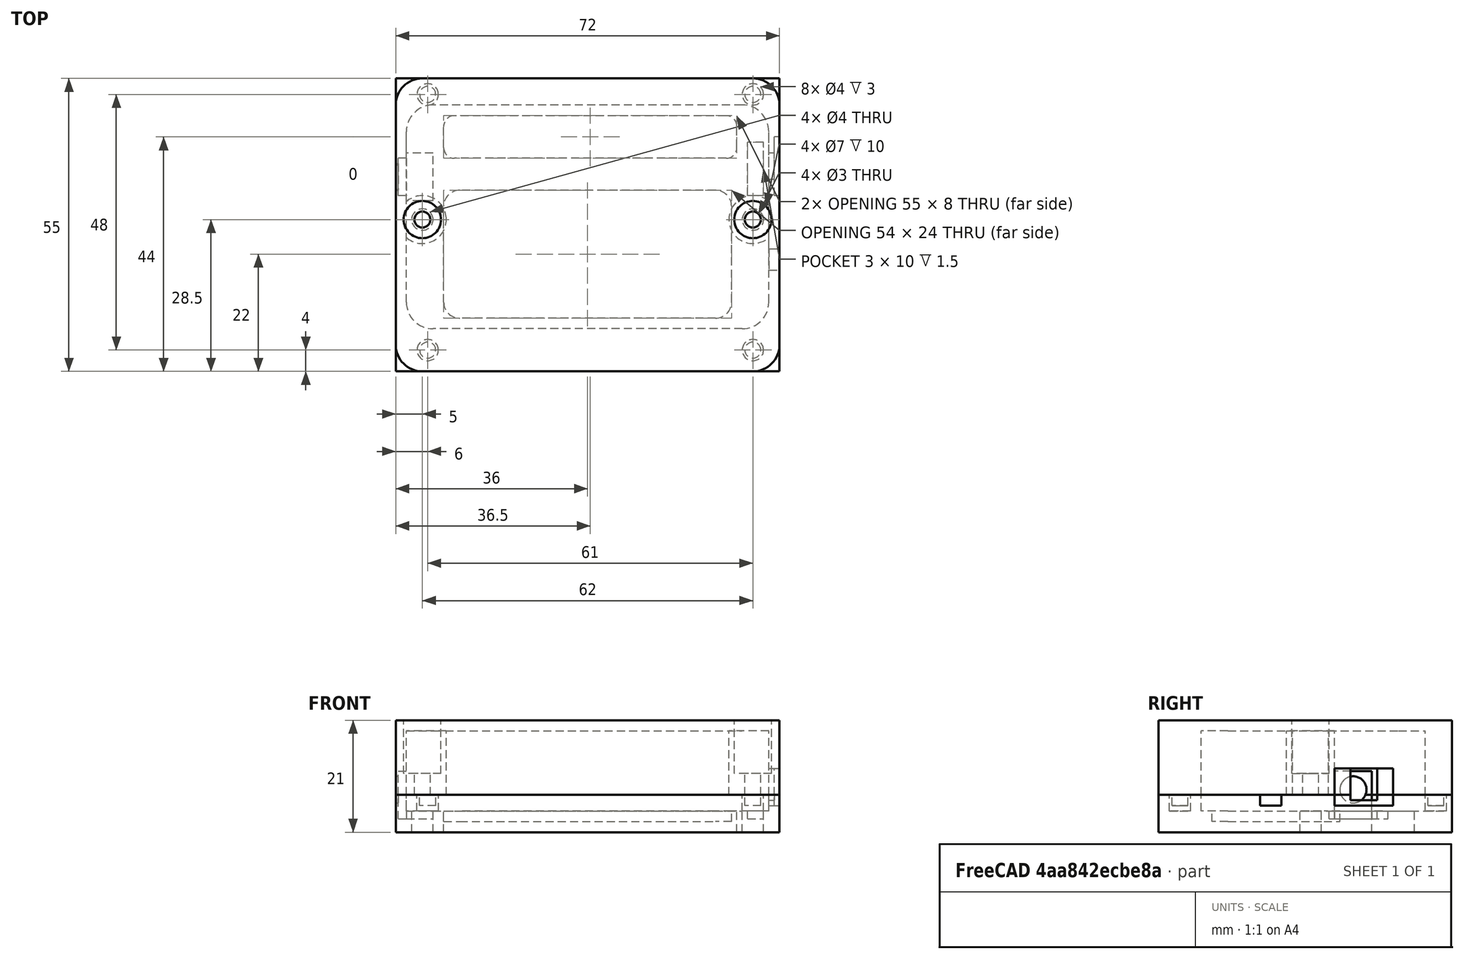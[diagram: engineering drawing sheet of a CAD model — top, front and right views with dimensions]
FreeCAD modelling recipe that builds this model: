
FCSTD DOCUMENT  (FreeCAD 0.19R19667 (Git))
Label: FieldTesterEnclosure
License: All rights reserved
LicenseURL: http://en.wikipedia.org/wiki/All_rights_reserved
objects: Part::Cylinder×36, Part::Box×30, Part::Cut×28, Part::MultiFuse×20, Part::Fillet×10
note: 124 computed .brp shape members not serialized (recipe doc carries the construction recipe); baked Part::Feature solids carry a one-line shape summary decoded from their .brp

FEATURE [Part::Box] Box  label="Cube"
  AttacherType = Attacher::AttachEngine3D
  Height = 7
  Length = 72
  Placement = pos=(-1,0,0) rot=(0,0,1;0rad)
  Width = 55
FEATURE [Part::Box] Box001  label="Cube001"
  AttacherType = Attacher::AttachEngine3D
  Height = 4
  Length = 68
  Placement = pos=(1,8,4) rot=(0,0,1;0rad)
  Width = 42
FEATURE [Part::Box] Box002  label="Cube002"
  AttacherType = Attacher::AttachEngine3D
  Height = 6
  Length = 55
  Placement = pos=(8,40,-2) rot=(0,0,1;0rad)
  Width = 8
FEATURE [Part::Fillet] Fillet
  Base = -> Box001
  Edges = 4 edges r=5: [Edge1,Edge3,Edge5,Edge7]
FEATURE [Part::Fillet] Fillet001
  Base = -> Box002
  Edges = 4 edges r=2: [Edge1,Edge3,Edge5,Edge7]
FEATURE [Part::Cut] Cut
  Base = -> Box
  Tool = -> Fillet
FEATURE [Part::Cut] Cut001
  Base = -> Cut
  Tool = -> Fillet001
FEATURE [Part::Box] Box003  label="antenne"
  AttacherType = Attacher::AttachEngine3D
  Height = 6
  Length = 2
  Placement = pos=(-0.5,33,2.5) rot=(0,0,1;0rad)
  Width = 7
FEATURE [Part::Cylinder] Cylinder
  Angle = 360
  AttacherType = Attacher::AttachEngine3D
  Height = 3
  Placement = pos=(-2,36.5,8) rot=(0,1,0;1.5708rad)
  Radius = 2.5
FEATURE [Part::MultiFuse] Fusion  label="Antenne"
  Shapes = -> [Box003,Cylinder]
FEATURE [Part::Cut] Cut002
  Base = -> Cut001
  Tool = -> Fusion
FEATURE [Part::Cylinder] Cylinder001
  Angle = 360
  AttacherType = Attacher::AttachEngine3D
  Height = 10
  Placement = pos=(4,28.5,-2) rot=(0,0,1;0rad)
  Radius = 2
FEATURE [Part::Cylinder] Cylinder002
  Angle = 360
  AttacherType = Attacher::AttachEngine3D
  Height = 10
  Placement = pos=(66,28.5,-2) rot=(0,0,1;0rad)
  Radius = 2
FEATURE [Part::MultiFuse] Fusion001  label="Holes"
  Shapes = -> [Cylinder001,Cylinder002]
FEATURE [Part::Cut] Cut003
  Base = -> Cut002
  Tool = -> Fusion001
FEATURE [Part::Box] Box004  label="bouton"
  AttacherType = Attacher::AttachEngine3D
  Height = 6
  Length = 2
  Placement = pos=(69,36,6) rot=(0,0,1;0rad)
  Width = 5
FEATURE [Part::Box] Box005  label="bouton2"
  AttacherType = Attacher::AttachEngine3D
  Height = 6
  Length = 1
  Placement = pos=(70,33,5) rot=(0,0,1;0rad)
  Width = 11
FEATURE [Part::MultiFuse] Fusion002  label="Bouton"
  Shapes = -> [Box004,Box005]
FEATURE [Part::Cut] Cut004
  Base = -> Cut003
  Tool = -> Fusion002
FEATURE [Part::Cylinder] Cylinder003
  Angle = 360
  AttacherType = Attacher::AttachEngine3D
  Height = 5
  Placement = pos=(5,4,4) rot=(0,0,1;0rad)
  Radius = 2
FEATURE [Part::Cylinder] Cylinder004
  Angle = 360
  AttacherType = Attacher::AttachEngine3D
  Height = 5
  Placement = pos=(66,4,4) rot=(0,0,1;0rad)
  Radius = 2
FEATURE [Part::Cylinder] Cylinder005
  Angle = 360
  AttacherType = Attacher::AttachEngine3D
  Height = 5
  Placement = pos=(66,52,4) rot=(0,0,1;0rad)
  Radius = 2
FEATURE [Part::Cylinder] Cylinder006
  Angle = 360
  AttacherType = Attacher::AttachEngine3D
  Height = 5
  Placement = pos=(5,52,4) rot=(0,0,1;0rad)
  Radius = 2
FEATURE [Part::MultiFuse] Fusion003  label="attache"
  Shapes = -> [Cylinder003,Cylinder004,Cylinder005,Cylinder006]
FEATURE [Part::Cut] Cut005
  Base = -> Cut004
  Tool = -> Fusion003
FEATURE [Part::Box] Box013  label="led"
  AttacherType = Attacher::AttachEngine3D
  Height = 2
  Length = 3
  Placement = pos=(68,19,5) rot=(0,0,1;0rad)
  Width = 4
FEATURE [Part::Cut] Cut012
  Base = -> Cut005
  Tool = -> Box013
FEATURE [Part::Box] Box014  label="Cube008"
  AttacherType = Attacher::AttachEngine3D
  Height = 3
  Length = 54
  Placement = pos=(8,10,2) rot=(0,0,1;0rad)
  Width = 24
FEATURE [Part::Fillet] Fillet002
  Base = -> Box014
  Edges = 4 edges r=3: [Edge1,Edge3,Edge5,Edge7]
FEATURE [Part::Box] Box015  label="Cube009"
  AttacherType = Attacher::AttachEngine3D
  Height = 2
  Length = 3
  Placement = pos=(65,33,2.5) rot=(0,0,1;0rad)
  Width = 10
FEATURE [Part::Box] Box016  label="Cube010"
  AttacherType = Attacher::AttachEngine3D
  Height = 2
  Length = 5
  Placement = pos=(1,32,2.5) rot=(0,0,1;0rad)
  Width = 9
FEATURE [Part::MultiFuse] Fusion004
  Shapes = -> [Fillet002,Box015,Box016]
FEATURE [Part::Cut] Cut013  label="dessous-sans-fillet"
  Base = -> Cut012
  Tool = -> Fusion004
FEATURE [Part::Cylinder] Cylinder007
  Angle = 360
  AttacherType = Attacher::AttachEngine3D
  Height = 3
  Placement = pos=(-2,36.5,8) rot=(0,1,0;1.5708rad)
  Radius = 2.5
FEATURE [Part::Box] Box017  label="Cube011"
  AttacherType = Attacher::AttachEngine3D
  Height = 6
  Length = 55
  Placement = pos=(8,40,-2) rot=(0,0,1;0rad)
  Width = 8
FEATURE [Part::Box] Box018  label="bouton003"
  AttacherType = Attacher::AttachEngine3D
  Height = 6
  Length = 2
  Placement = pos=(69,36,6) rot=(0,0,1;0rad)
  Width = 5
FEATURE [Part::Box] Box019  label="bouton004"
  AttacherType = Attacher::AttachEngine3D
  Height = 6
  Length = 1
  Placement = pos=(70,33,5) rot=(0,0,1;0rad)
  Width = 11
FEATURE [Part::MultiFuse] Fusion005  label="Bouton001"
  Shapes = -> [Box018,Box019]
FEATURE [Part::Box] Box020  label="Cube012"
  AttacherType = Attacher::AttachEngine3D
  Height = 2
  Length = 5
  Placement = pos=(1,32,2.5) rot=(0,0,1;0rad)
  Width = 9
FEATURE [Part::Cylinder] Cylinder008
  Angle = 360
  AttacherType = Attacher::AttachEngine3D
  Height = 10
  Placement = pos=(4,28.5,-2) rot=(0,0,1;0rad)
  Radius = 2
FEATURE [Part::Cylinder] Cylinder009
  Angle = 360
  AttacherType = Attacher::AttachEngine3D
  Height = 5
  Placement = pos=(66,4,4) rot=(0,0,1;0rad)
  Radius = 2
FEATURE [Part::Cylinder] Cylinder010
  Angle = 360
  AttacherType = Attacher::AttachEngine3D
  Height = 5
  Placement = pos=(5,52,4) rot=(0,0,1;0rad)
  Radius = 2
FEATURE [Part::Cylinder] Cylinder011
  Angle = 360
  AttacherType = Attacher::AttachEngine3D
  Height = 5
  Placement = pos=(66,52,4) rot=(0,0,1;0rad)
  Radius = 2
FEATURE [Part::Box] Box021  label="Cube013"
  AttacherType = Attacher::AttachEngine3D
  Height = 2
  Length = 3
  Placement = pos=(65,33,2.5) rot=(0,0,1;0rad)
  Width = 10
FEATURE [Part::Box] Box022  label="antenne001"
  AttacherType = Attacher::AttachEngine3D
  Height = 6
  Length = 2
  Placement = pos=(-0.5,33,2.5) rot=(0,0,1;0rad)
  Width = 7
FEATURE [Part::Fillet] Fillet005
  Base = -> Box017
  Edges = 4 edges r=2: [Edge1,Edge3,Edge5,Edge7]
FEATURE [Part::Cylinder] Cylinder012
  Angle = 360
  AttacherType = Attacher::AttachEngine3D
  Height = 5
  Placement = pos=(5,4,4) rot=(0,0,1;0rad)
  Radius = 2
FEATURE [Part::Box] Box023  label="Cube014"
  AttacherType = Attacher::AttachEngine3D
  Height = 4
  Length = 68
  Placement = pos=(1,8,4) rot=(0,0,1;0rad)
  Width = 42
FEATURE [Part::Fillet] Fillet003
  Base = -> Box023
  Edges = 4 edges r=5: [Edge1,Edge3,Edge5,Edge7]
FEATURE [Part::Box] Box024  label="Cube015"
  AttacherType = Attacher::AttachEngine3D
  Height = 7
  Length = 72
  Placement = pos=(-1,0,0) rot=(0,0,1;0rad)
  Width = 55
FEATURE [Part::Cut] Cut014
  Base = -> Box024
  Tool = -> Fillet003
FEATURE [Part::Cylinder] Cylinder013
  Angle = 360
  AttacherType = Attacher::AttachEngine3D
  Height = 10
  Placement = pos=(66,28.5,-2) rot=(0,0,1;0rad)
  Radius = 2
FEATURE [Part::Box] Box025  label="Cube016"
  AttacherType = Attacher::AttachEngine3D
  Height = 3
  Length = 54
  Placement = pos=(8,10,2) rot=(0,0,1;0rad)
  Width = 24
FEATURE [Part::Fillet] Fillet004
  Base = -> Box025
  Edges = 4 edges r=3: [Edge1,Edge3,Edge5,Edge7]
FEATURE [Part::Box] Box026  label="led001"
  AttacherType = Attacher::AttachEngine3D
  Height = 2
  Length = 3
  Placement = pos=(68,19,5) rot=(0,0,1;0rad)
  Width = 4
FEATURE [Part::MultiFuse] Fusion006
  Shapes = -> [Fillet004,Box021,Box020]
FEATURE [Part::MultiFuse] Fusion007  label="attache001"
  Shapes = -> [Cylinder012,Cylinder009,Cylinder011,Cylinder010]
FEATURE [Part::MultiFuse] Fusion008  label="Holes001"
  Shapes = -> [Cylinder008,Cylinder013]
FEATURE [Part::Cut] Cut021
  Base = -> Cut014
  Tool = -> Fillet005
FEATURE [Part::MultiFuse] Fusion009  label="Antenne001"
  Shapes = -> [Box022,Cylinder007]
FEATURE [Part::Cut] Cut015
  Base = -> Cut021
  Tool = -> Fusion009
FEATURE [Part::Cut] Cut020
  Base = -> Cut015
  Tool = -> Fusion008
FEATURE [Part::Cut] Cut016
  Base = -> Cut020
  Tool = -> Fusion005
FEATURE [Part::Cut] Cut017
  Base = -> Cut016
  Tool = -> Fusion007
FEATURE [Part::Cut] Cut018
  Base = -> Cut017
  Tool = -> Box026
FEATURE [Part::Cut] Cut019
  Base = -> Cut018
  Tool = -> Fusion006
FEATURE [Part::Fillet] Fillet006  label="Dessous-avec-fillet"
  Base = -> Cut019
  Edges = 4 edges r=5: [Edge5,Edge7,Edge40,Edge53]
FEATURE [Part::Box] Box027  label="Cube017"
  AttacherType = Attacher::AttachEngine3D
  Height = 14
  Length = 72
  Placement = pos=(-1,0,7) rot=(0,0,1;0rad)
  Width = 55
FEATURE [Part::Cylinder] Cylinder014
  Angle = 360
  AttacherType = Attacher::AttachEngine3D
  Height = 5
  Placement = pos=(5,4,5) rot=(0,0,1;0rad)
  Radius = 1.5
FEATURE [Part::Cylinder] Cylinder015
  Angle = 360
  AttacherType = Attacher::AttachEngine3D
  Height = 5
  Placement = pos=(66,4,5) rot=(0,0,1;0rad)
  Radius = 1.5
FEATURE [Part::Cylinder] Cylinder016
  Angle = 360
  AttacherType = Attacher::AttachEngine3D
  Height = 5
  Placement = pos=(66,52,5) rot=(0,0,1;0rad)
  Radius = 1.5
FEATURE [Part::Cylinder] Cylinder017
  Angle = 360
  AttacherType = Attacher::AttachEngine3D
  Height = 5
  Placement = pos=(5,52,5) rot=(0,0,1;0rad)
  Radius = 1.5
FEATURE [Part::Box] Box028  label="antenne002"
  AttacherType = Attacher::AttachEngine3D
  Height = 6
  Length = 2
  Placement = pos=(-0.5,33,5.5) rot=(0,0,1;0rad)
  Width = 7
FEATURE [Part::Cylinder] Cylinder018
  Angle = 360
  AttacherType = Attacher::AttachEngine3D
  Height = 3
  Placement = pos=(-2,36.5,8) rot=(0,1,0;1.5708rad)
  Radius = 2.5
FEATURE [Part::Box] Box029  label="Cube018"
  AttacherType = Attacher::AttachEngine3D
  Height = 12
  Length = 68
  Placement = pos=(1,8,7) rot=(0,0,1;0rad)
  Width = 42
FEATURE [Part::Fillet] Fillet007
  Base = -> Box029
  Edges = 4 edges r=5: [Edge1,Edge3,Edge5,Edge7]
FEATURE [Part::Cut] Cut022
  Base = -> Box027
  Tool = -> Fillet007
FEATURE [Part::MultiFuse] Fusion010  label="Attache"
  Shapes = -> [Cylinder014,Cylinder015,Cylinder016,Cylinder017]
FEATURE [Part::MultiFuse] Fusion011  label="Antenne002"
  Shapes = -> [Box028,Cylinder018]
FEATURE [Part::Box] Box030  label="bouton005"
  AttacherType = Attacher::AttachEngine3D
  Height = 5
  Length = 2
  Placement = pos=(69,36,7) rot=(0,0,1;0rad)
  Width = 5
FEATURE [Part::Box] Box031  label="bouton006"
  AttacherType = Attacher::AttachEngine3D
  Height = 5
  Length = 1
  Placement = pos=(70,33,7) rot=(0,0,1;0rad)
  Width = 11
FEATURE [Part::MultiFuse] Fusion012  label="Interrupteur"
  Shapes = -> [Box030,Box031]
FEATURE [Part::Cylinder] Cylinder019
  Angle = 360
  AttacherType = Attacher::AttachEngine3D
  Height = 20
  Placement = pos=(4,28.5,5) rot=(0,0,1;0rad)
  Radius = 1.5
FEATURE [Part::Cylinder] Cylinder020
  Angle = 360
  AttacherType = Attacher::AttachEngine3D
  Height = 16
  Placement = pos=(66,28.5,6) rot=(0,0,1;0rad)
  Radius = 1.5
FEATURE [Part::Cylinder] Cylinder021
  Angle = 360
  AttacherType = Attacher::AttachEngine3D
  Height = 14
  Placement = pos=(4,28.5,7) rot=(0,0,1;0rad)
  Radius = 4.5
FEATURE [Part::Cylinder] Cylinder022
  Angle = 360
  AttacherType = Attacher::AttachEngine3D
  Height = 14
  Placement = pos=(66,28.5,7) rot=(0,0,1;0rad)
  Radius = 4.5
FEATURE [Part::Cut] Cut023
  Base = -> Cylinder022
  Tool = -> Cylinder020
FEATURE [Part::Cut] Cut024
  Base = -> Cylinder021
  Tool = -> Cylinder019
FEATURE [Part::Cut] Cut025
  Base = -> Cut022
  Tool = -> Fusion011
FEATURE [Part::Cut] Cut026
  Base = -> Cut025
  Tool = -> Fusion012
FEATURE [Part::MultiFuse] Fusion013
  Shapes = -> [Cut026,Fusion010,Cut023,Cut024]
FEATURE [Part::Cylinder] Cylinder025
  Angle = 360
  AttacherType = Attacher::AttachEngine3D
  Height = 16
  Placement = pos=(66,28.5,11) rot=(0,0,1;0rad)
  Radius = 3.5
FEATURE [Part::Cylinder] Cylinder026
  Angle = 360
  AttacherType = Attacher::AttachEngine3D
  Height = 20
  Placement = pos=(4,28.5,11) rot=(0,0,1;0rad)
  Radius = 3.5
FEATURE [Part::MultiFuse] Fusion014
  Shapes = -> [Cylinder025,Cylinder026]
FEATURE [Part::Cut] Cut027  label="Dessus-sans-fillet"
  Base = -> Fusion013
  Tool = -> Fusion014
FEATURE [Part::Box] Box032  label="Cube019"
  AttacherType = Attacher::AttachEngine3D
  Height = 14
  Length = 72
  Placement = pos=(-1,0,7) rot=(0,0,1;0rad)
  Width = 55
FEATURE [Part::Box] Box033  label="Cube020"
  AttacherType = Attacher::AttachEngine3D
  Height = 12
  Length = 68
  Placement = pos=(1,8,7) rot=(0,0,1;0rad)
  Width = 42
FEATURE [Part::Box] Box034  label="bouton007"
  AttacherType = Attacher::AttachEngine3D
  Height = 5
  Length = 2
  Placement = pos=(69,36,7) rot=(0,0,1;0rad)
  Width = 5
FEATURE [Part::Cylinder] Cylinder027
  Angle = 360
  AttacherType = Attacher::AttachEngine3D
  Height = 20
  Placement = pos=(4,28.5,11) rot=(0,0,1;0rad)
  Radius = 3.5
FEATURE [Part::Fillet] Fillet008
  Base = -> Box033
  Edges = 4 edges r=5: [Edge1,Edge3,Edge5,Edge7]
FEATURE [Part::Cylinder] Cylinder028
  Angle = 360
  AttacherType = Attacher::AttachEngine3D
  Height = 14
  Placement = pos=(66,28.5,7) rot=(0,0,1;0rad)
  Radius = 4.5
FEATURE [Part::Cylinder] Cylinder029
  Angle = 360
  AttacherType = Attacher::AttachEngine3D
  Height = 16
  Placement = pos=(66,28.5,11) rot=(0,0,1;0rad)
  Radius = 3.5
FEATURE [Part::MultiFuse] Fusion016
  Shapes = -> [Cylinder029,Cylinder027]
FEATURE [Part::Box] Box035  label="antenne003"
  AttacherType = Attacher::AttachEngine3D
  Height = 6
  Length = 2
  Placement = pos=(-0.5,33,5.5) rot=(0,0,1;0rad)
  Width = 7
FEATURE [Part::Cylinder] Cylinder030
  Angle = 360
  AttacherType = Attacher::AttachEngine3D
  Height = 3
  Placement = pos=(-2,36.5,8) rot=(0,1,0;1.5708rad)
  Radius = 2.5
FEATURE [Part::MultiFuse] Fusion018  label="Antenne003"
  Shapes = -> [Box035,Cylinder030]
FEATURE [Part::Box] Box036  label="bouton008"
  AttacherType = Attacher::AttachEngine3D
  Height = 5
  Length = 1
  Placement = pos=(70,33,7) rot=(0,0,1;0rad)
  Width = 11
FEATURE [Part::MultiFuse] Fusion017  label="Interrupteur001"
  Shapes = -> [Box034,Box036]
FEATURE [Part::Cylinder] Cylinder031
  Angle = 360
  AttacherType = Attacher::AttachEngine3D
  Height = 20
  Placement = pos=(4,28.5,5) rot=(0,0,1;0rad)
  Radius = 1.5
FEATURE [Part::Cylinder] Cylinder032
  Angle = 360
  AttacherType = Attacher::AttachEngine3D
  Height = 16
  Placement = pos=(66,28.5,6) rot=(0,0,1;0rad)
  Radius = 1.5
FEATURE [Part::Cut] Cut029
  Base = -> Cylinder028
  Tool = -> Cylinder032
FEATURE [Part::Cut] Cut032
  Base = -> Box032
  Tool = -> Fillet008
FEATURE [Part::Cylinder] Cylinder033
  Angle = 360
  AttacherType = Attacher::AttachEngine3D
  Height = 14
  Placement = pos=(4,28.5,7) rot=(0,0,1;0rad)
  Radius = 4.5
FEATURE [Part::Cut] Cut030
  Base = -> Cylinder033
  Tool = -> Cylinder031
FEATURE [Part::Cut] Cut033
  Base = -> Cut032
  Tool = -> Fusion018
FEATURE [Part::Cut] Cut028
  Base = -> Cut033
  Tool = -> Fusion017
FEATURE [Part::Cylinder] Cylinder034
  Angle = 360
  AttacherType = Attacher::AttachEngine3D
  Height = 5
  Placement = pos=(5,4,5) rot=(0,0,1;0rad)
  Radius = 1.5
FEATURE [Part::Cylinder] Cylinder035
  Angle = 360
  AttacherType = Attacher::AttachEngine3D
  Height = 5
  Placement = pos=(66,4,5) rot=(0,0,1;0rad)
  Radius = 1.5
FEATURE [Part::Cylinder] Cylinder036
  Angle = 360
  AttacherType = Attacher::AttachEngine3D
  Height = 5
  Placement = pos=(5,52,5) rot=(0,0,1;0rad)
  Radius = 1.5
FEATURE [Part::Cylinder] Cylinder037
  Angle = 360
  AttacherType = Attacher::AttachEngine3D
  Height = 5
  Placement = pos=(66,52,5) rot=(0,0,1;0rad)
  Radius = 1.5
FEATURE [Part::MultiFuse] Fusion015  label="Attache001"
  Shapes = -> [Cylinder034,Cylinder035,Cylinder037,Cylinder036]
FEATURE [Part::MultiFuse] Fusion019
  Shapes = -> [Cut028,Fusion015,Cut029,Cut030]
FEATURE [Part::Cut] Cut031  label="Dessus-sans-fillet001"
  Base = -> Fusion019
  Tool = -> Fusion016
FEATURE [Part::Fillet] Fillet009  label="Dessus-avec-filet"
  Base = -> Cut031
  Edges = 4 edges r=5: [Edge2,Edge6,Edge13,Edge49]
